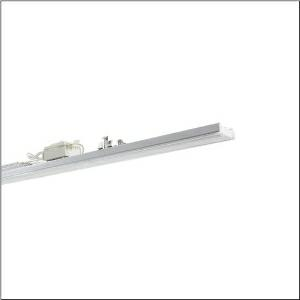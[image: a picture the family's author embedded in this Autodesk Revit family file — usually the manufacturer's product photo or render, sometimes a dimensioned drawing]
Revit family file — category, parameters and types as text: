
# Revit family: licross_11_recessed_ho_51tl12dv4m2m3s
name_source: partatom
category: Lighting Fixtures
units: mm (PartAtom-declared; Revit-internal decimal feet)

## family parameters
Cut with Voids When Loaded = No
Host = Face
Light Source = No
Part Type = Normal
Room Calculation Point = No
Round Connector Dimension = Use Diameter
Shared = No

## types (1)
- --- (1 x LED, 1010 lm, 5.9 W, 4000K)
    Apparent Load = 6 VA
    CIE Flux Codes = 66 91 98 100 100
    Color Rendering = 80
    Color Temperature = 4000K
    Default Elevation = 1800 mm
    Description = Licross 11 Recessed HO, luminaire insert, of sheet steel, coil coated, white, length: 2.250mm, width: 66mm, height: 67mm, LED rated luminous flux: 27.150lm, light colour: 840, SDCM (Standard Deviation of Colour Matching)MacAdam ≤ 2 SDCM (initial), control gear: DALI 2 (for two DALI lines), with plug, 6-pole, with phase selection, for trunking rail, 14-core, mains connection: 220..240V, AC, 50/60Hz, rated input power: 154W, for trunking rail, 14-core, internal wiring halogen-free, for emergency light function, converter,control gear: single battery element, battery: LiFePO4, 9Ah, primary optical cover: cover, of PMMA, light emission: direct distribution, primary light characteristic: symmetric, protection rating (complete): IP40, insulation class (complete): insulation class I (protective earthing), certification: CE, UKCA, protection symbol: D if used in an environment without relevant dust loads with corresponding accessories, impact resistance: IK06, permissible ambient temperature for indoor applications: +5..+35°C, standard: EN 60598-2-22, LABS conformity tested according to VDMA 24364:2018-05, reducing of maximum allowable ambient temperature of 5°C with ceiling mounting, corresponds to IFS (International Featured Standards) requirements for safety and quality in the food industry, The light source and the operating device comply with the requirements of the Ecodesign Regulation (EU) 2019/2020 and are replaceable in accordance with this regulation, packaging unit: 1 piece
    Height = 58 mm
    Lamp = 1 x LED
    Lamp Light Flux = 1010 lm
    Lamp Power = 5.9 W
    Lamp count = 1
    Length = 2250 mm
    Luminous efficacy = 171 lm/W
    Manufacturer = Siteco
    ModVariant = No
    Model = 51TL12DV4M2M3S
    Mounting Place = Ceiling
    Mounting Type = Pendant
    Number of Poles = 1
    OnlyDefault = Yes
    Power Factor = 1
    Product Name = Licross 11 Recessed HO
    Product group = luminaire insert | ceiling pendant
    ProductGroupID = 901
    Protection Class = Protection class I
    Protection Degree = IP 40
    RLX_Detail_Level = 1
    RLX_Emergency_Light_Flux = 0 lm
    RLX_Emergency_Type = 0
    RLX_Emergency_Type_DB = No
    RlxData = <blob elided: 30257 chars, md5=e0083a96>
    Socket = socket
    Standby Power = 0 W
    System Light Flux = 1010 lm
    System Power = 6 W
    Type Comments = : emergency light operation: 3 h
    Type Image = l_1296930.jpg
    URL = http://relux.com
    VarID = @adj_089625
    Voltage = 0 V
    Weight = 0.00 kg
    Width = 66 mm

## geometry (parser evidence)
native form markers: Blend x4, Sweep x10
no freeform markers — native parametric forms only
